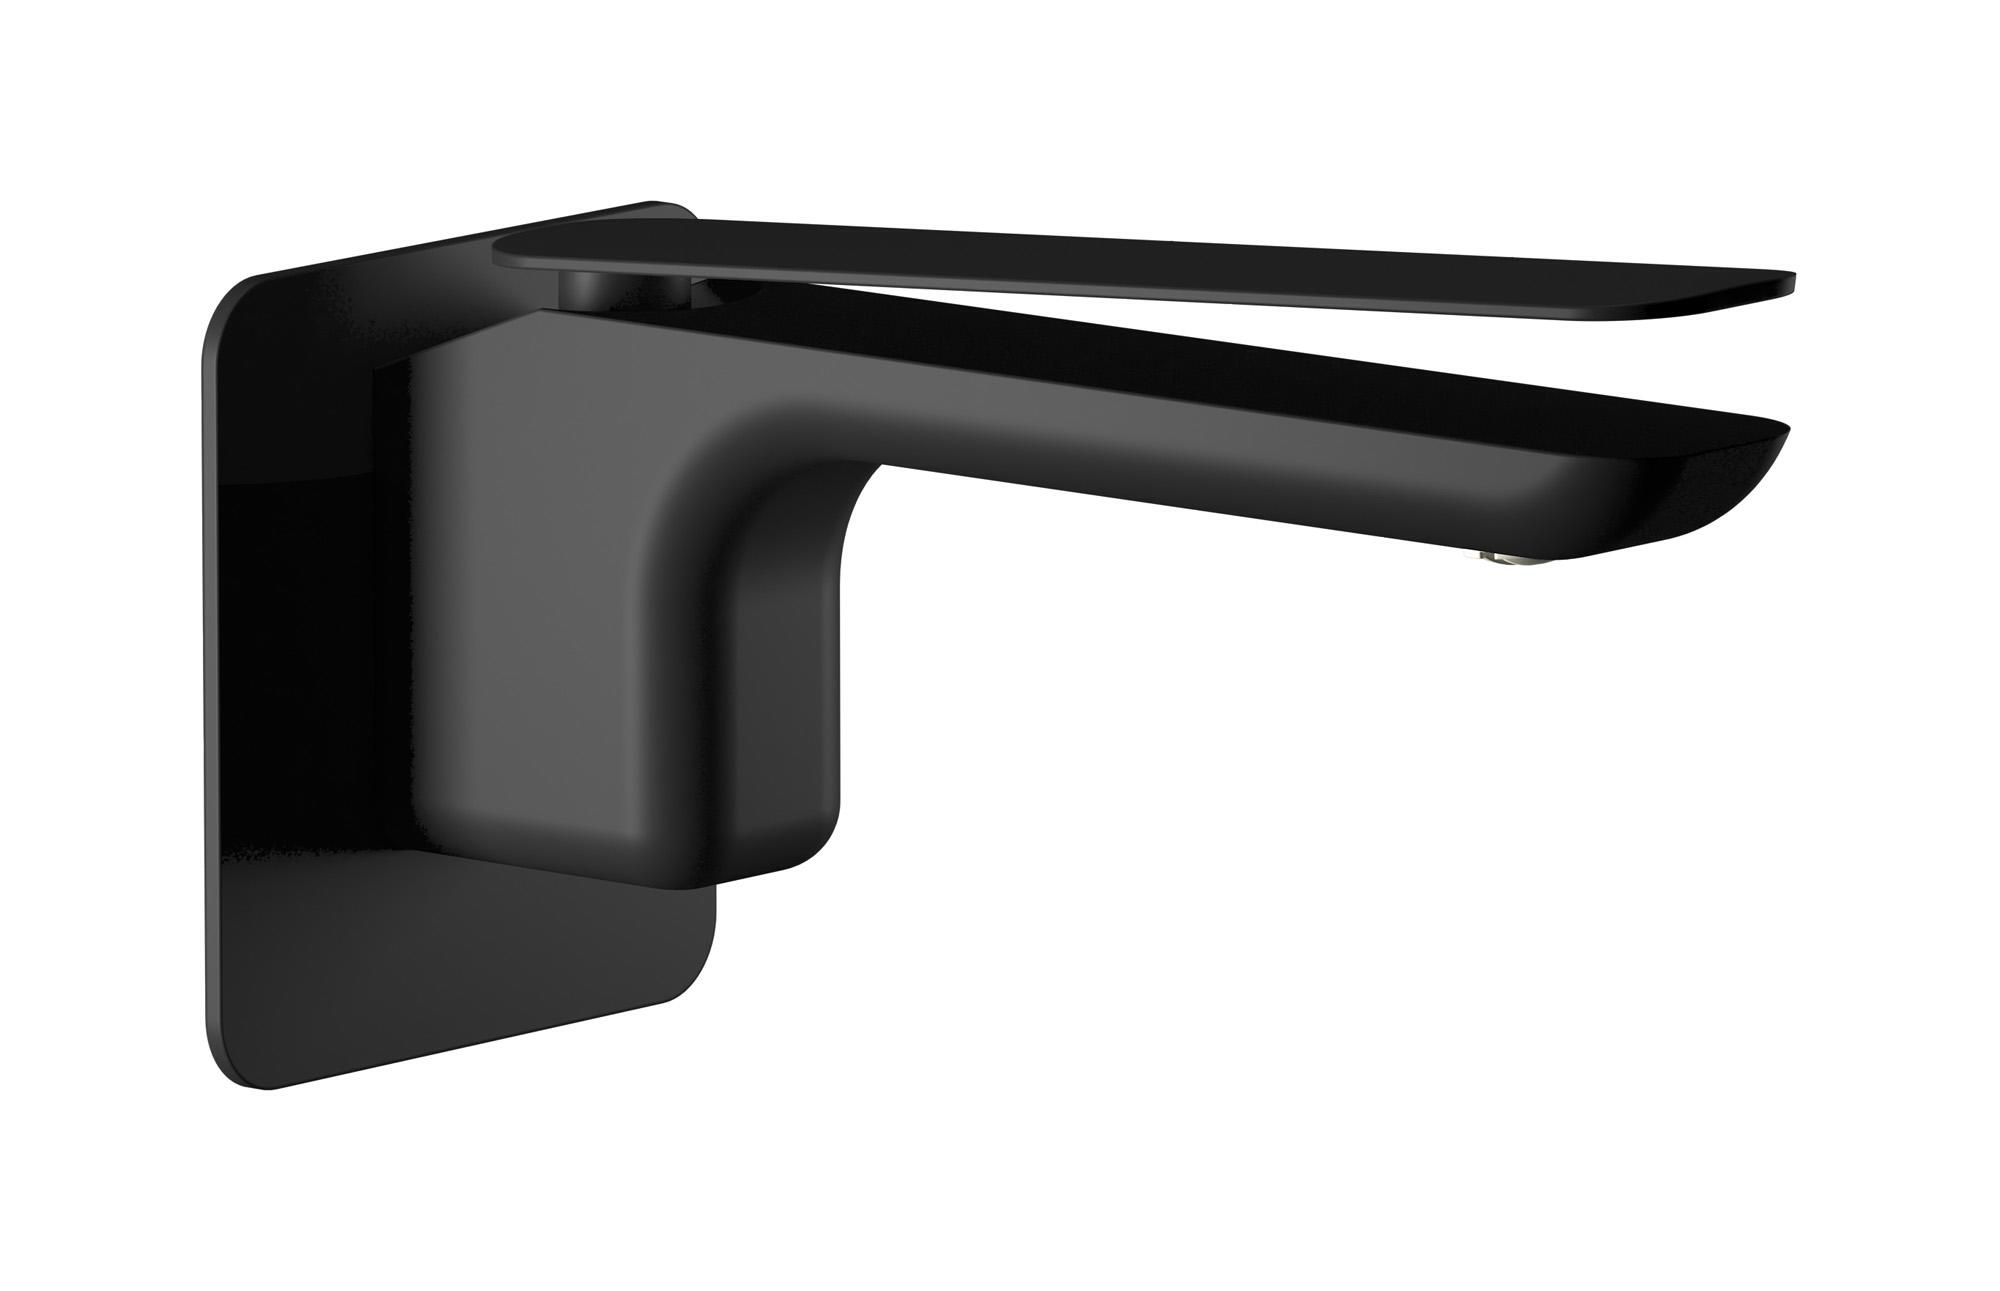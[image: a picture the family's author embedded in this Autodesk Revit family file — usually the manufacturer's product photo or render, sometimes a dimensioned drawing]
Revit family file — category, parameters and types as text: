
# Revit family: K2209
name_source: partatom
category: Apparecchi idraulici
units: mm (PartAtom-declared; Revit-internal decimal feet)

## family parameters
Basato su piano di lavoro = No
Condiviso = No
Mantieni orientamento annotazione = No
Numero OmniClass = 23.45.55.17
Punto di calcolo locali = No
Quota connettore circolare = Usa diametro
Sempre verticale = Sì
Taglio con vuoti quando caricato = No
Tipo di parte = Normale
Titolo OmniClass = Mixing Faucets

## types (9) — shared parameters
Cold water inlet = 10 mm  [stored 0.0328084 ft]
Commenti sul tipo = Washbasin mixer
Connessione CW = No
Connessione HW = No
Connessione di scarico = No
Connessione di ventilazione = No
Descrizione = Monohole wall mounted washbasin mixer
Hot water inlet = 10 mm  [stored 0.0328084 ft]
Produttore = IB Rubinetterie S.p.A.
URL = https://www.weareib.it
zero-valued in all types: Prospetto di default

## per-type parameters (varying)
| type | Finishes surface | Immagine tipo | Modello |
| Chrome | IB_Chrome | K2209CC.jpg | K2209CC |
| Platinum | IB_Platinum | K2209PL.jpg | K2209PL |
| Brushed nickel | IB_Brushed nickel | K2209SS.jpg | K2209SS |
| Matt black | IB_matt black | K2209NP.jpg | K2209NP |
| Matt white | IB_matt white | K2209BO.jpg | K2209BO |
| Pale gold | IB_Pale gold | K2209II.jpg | K2209II |
| Brushed pale gold | IB_brushed pale gold | K2209IS.jpg | K2209IS |
| Rose gold | IB_Rose gold | K2209RS.jpg | K2209RS |
| Gold | IB_gold | K2209OO.jpg | K2209OO |

note: [stored X ft] marks values corroborated as IEEE doubles in the binary element streams (Revit-internal decimal feet)
